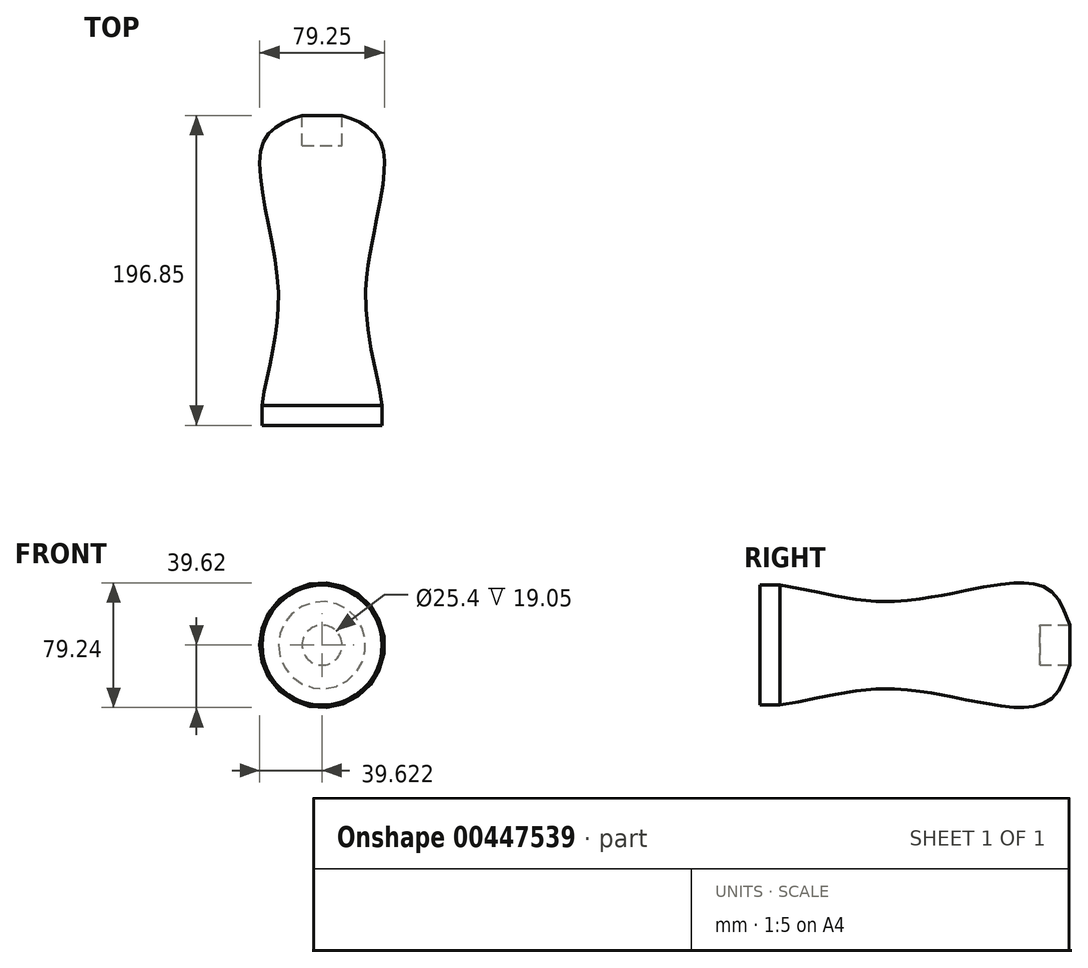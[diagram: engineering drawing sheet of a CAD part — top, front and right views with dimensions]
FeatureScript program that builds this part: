
annotation { "Feature Type Name" : "Feature", "Feature Type Description" : "" }
export const myFeature = defineFeature(function(context is Context, id is Id, definition is map)
    precondition{}
    {
        {
            var Q0;
            Q0=qCreatedBy(makeId("Top.planeOp"),FACE);
            var sketch = newSketch(context, id + "F0", { "sketchPlane" : qUnion([Q0])});
            skLineSegment(sketch, "E0", {"start": v(0.67, 0) * mm, "end": v(-37.43, 0) * mm});
            skLineSegment(sketch, "E1", {"start": v(-37.43, 0) * mm, "end": v(-37.43, 12.7) * mm});
            skLineSegment(sketch, "E2", {"start": v(0.67, 0) * mm, "end": v(0.67, 88.9) * mm, "construction": true});
            skLineSegment(sketch, "E3", {"start": v(0.67, 88.9) * mm, "end": v(0.67, 177.8) * mm, "construction": true});
            skLineSegment(sketch, "E4", {"start": v(0.67, 88.9) * mm, "end": v(-27.27, 88.9) * mm, "construction": true});
            skLineSegment(sketch, "E5", {"start": v(0.67, 177.8) * mm, "end": v(-37.43, 177.8) * mm, "construction": true});
            skLineSegment(sketch, "E6", {"start": v(0.67, 177.8) * mm, "end": v(0.67, 196.85) * mm, "construction": true});
            skLineSegment(sketch, "E7", {"start": v(0.67, 196.85) * mm, "end": v(-12.03, 196.85) * mm, "construction": true});
            skFitSpline(sketch, "E8", {"points": [v(-37.43, 12.7) * mm, v(-27.27, 88.9) * mm, v(-37.43, 177.8) * mm, v(-12.03, 196.85) * mm], "startDerivative": vector(28.47, 203.46) * mm, "endDerivative": vector(137.92, 46.53) * mm});
            skLineSegment(sketch, "E9", {"start": v(-12.03, 196.85) * mm, "end": v(-12.03, 177.8) * mm});
            skLineSegment(sketch, "E10", {"start": v(-12.03, 177.8) * mm, "end": v(0.67, 177.8) * mm});
            skLineSegment(sketch, "E11", {"start": v(0.67, 177.8) * mm, "end": v(0.67, 0) * mm});
            skSolve(sketch);
        }
        {
            var Q0;
            Q0=makeQuery(id+"F0.imprint","IMPRINT",FACE,{"disambiguationData":[TD([[makeQuery(id+"F0.imprint","IMPRINT",EDGE,{"derivedFrom":sQuery(id+"F0.wireOp",EDGE,"E0")}),-1.0]])]});
            var Q1;
            Q1=sQuery(id+"F0.wireOp",EDGE,"E11");
            revolve(context, id + "F1", {"entities" : qUnion([Q0]), "axis" : qUnion([Q1]), "revolveType" : RevolveType.FULL});
        }
    });
